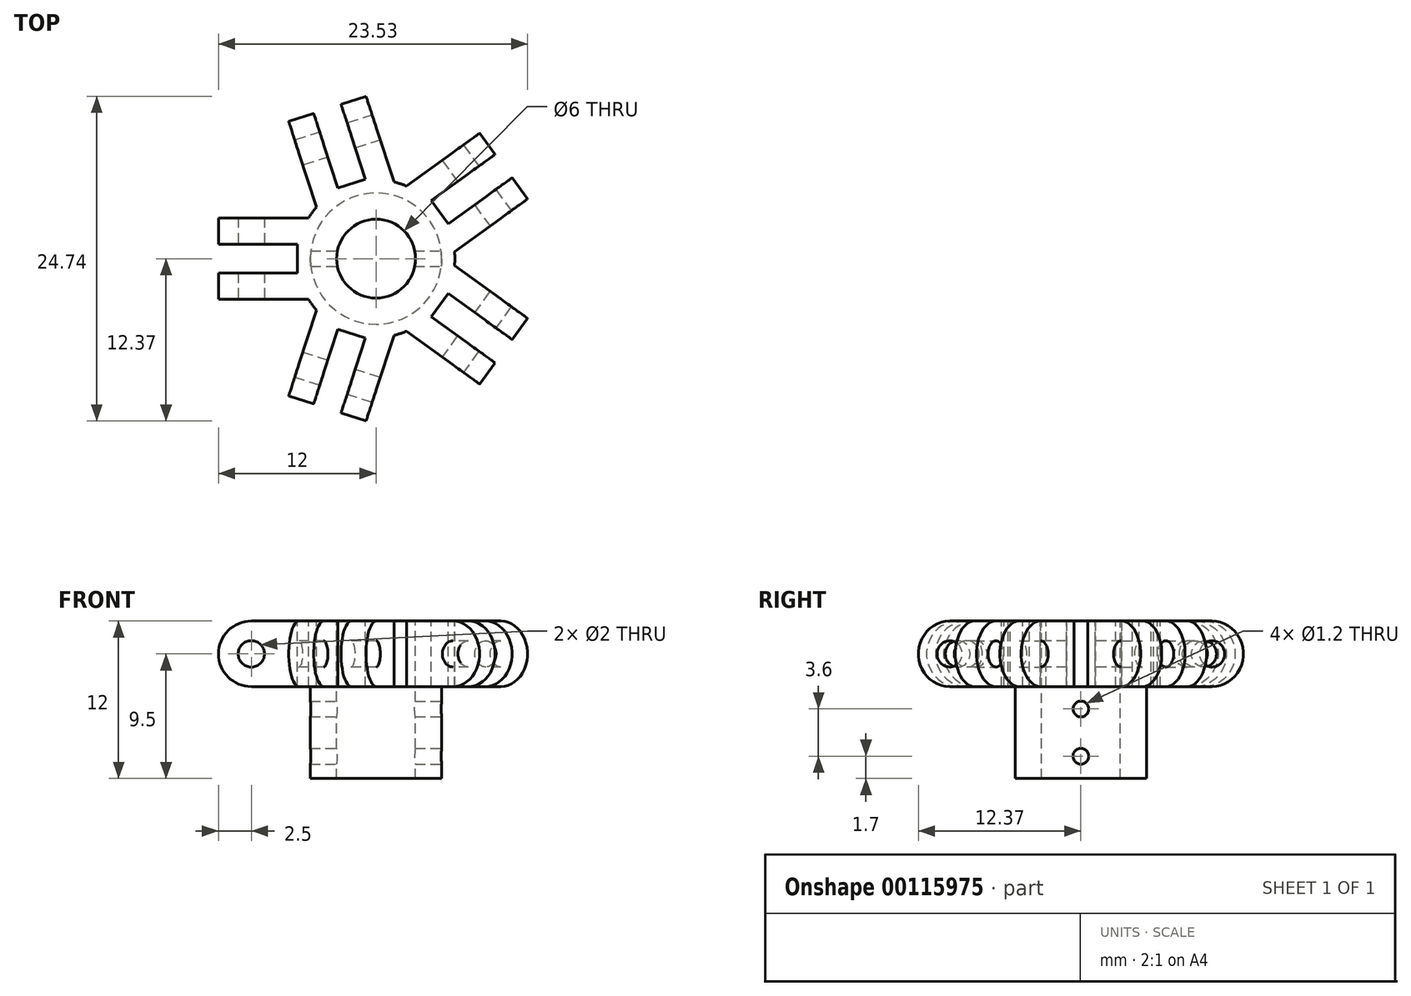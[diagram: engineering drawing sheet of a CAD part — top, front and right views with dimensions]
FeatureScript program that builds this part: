
annotation { "Feature Type Name" : "Feature", "Feature Type Description" : "" }
export const myFeature = defineFeature(function(context is Context, id is Id, definition is map)
    precondition{}
    {
        {
            var Q0;
            Q0=qCreatedBy(makeId("Front.planeOp"),FACE);
            var sketch = newSketch(context, id + "F0", { "sketchPlane" : qUnion([Q0])});
            skLineSegment(sketch, "E0", {"start": v(-3, 5) * mm, "end": v(-6, 5) * mm});
            skLineSegment(sketch, "E1", {"start": v(-6, 5) * mm, "end": v(-6, 0) * mm});
            skLineSegment(sketch, "E2", {"start": v(-6, 0) * mm, "end": v(-5, 0) * mm});
            skLineSegment(sketch, "E3", {"start": v(-5, 0) * mm, "end": v(-5, -7) * mm});
            skLineSegment(sketch, "E4", {"start": v(-5, -7) * mm, "end": v(-3, -7) * mm});
            skLineSegment(sketch, "E5", {"start": v(-3, -7) * mm, "end": v(-3, 5) * mm});
            skLineSegment(sketch, "E6", {"start": v(0, 11.9) * mm, "end": v(0, -21.79) * mm, "construction": true});
            skSolve(sketch);
        }
        {
            var Q0;
            Q0 = qSketchRegion(id + "F0", true);
            var Q1;
            Q1=sQuery(id+"F0.wireOp",EDGE,"E6");
            revolve(context, id + "F1", {"entities" : qUnion([Q0]), "axis" : qUnion([Q1]), "revolveType" : RevolveType.FULL});
        }
        {
            var Q0;
            Q0=qCreatedBy(makeId("Front.planeOp"),FACE);
            var sketch = newSketch(context, id + "F2", { "sketchPlane" : qUnion([Q0])});
            skLineSegment(sketch, "E7", {"start": v(-9.5, 5) * mm, "end": v(-5, 5) * mm});
            skLineSegment(sketch, "E8", {"start": v(-5, 5) * mm, "end": v(-5, 0) * mm});
            skLineSegment(sketch, "E9", {"start": v(-5, 0) * mm, "end": v(-9.5, 0) * mm});
            skLineSegment(sketch, "E10", {"start": v(-9.5, 0) * mm, "end": v(-9.5, 5) * mm, "construction": true});
            skArc(sketch, "E11", {"start": v(-9.5, 5) * mm, "mid": v(-12, 2.5) * mm, "end": v(-9.5, 0) * mm});
            skCircle(sketch, "E12", {"center": v(-9.5, 2.5) * mm, "radius": 2.5 * mm});
            skSolve(sketch);
        }
        {
            var Q0;
            Q0 = qSketchRegion(id + "F2", true);
            extrude(context, id + "F3", {"entities" : qUnion([Q0]), "endBound" : BoundingType.SYMMETRIC, "depth" : 6.2 * mm});
        }
        {
            var Q0;
            Q0=makeQuery(id+"F3.opExtrude","CAP_FACE",FACE,{"disambiguationData":[OSD([sQuery(id+"F2.wireOp",EDGE,"E7"),sQuery(id+"F2.wireOp",EDGE,"E8"),sQuery(id+"F2.wireOp",EDGE,"E9"),sQuery(id+"F2.wireOp",EDGE,"E12")])],"isStart":false});
            var sketch = newSketch(context, id + "F4", { "sketchPlane" : qUnion([Q0])});
            skCircle(sketch, "E13", {"center": v(-9.5, 2.5) * mm, "radius": 1 * mm});
            skSolve(sketch);
        }
        {
            var Q0;
            Q0=makeQuery(id+"F4.imprint","IMPRINT",FACE,{"disambiguationData":[TD([[makeQuery(id+"F4.imprint","IMPRINT",EDGE,{"derivedFrom":sQuery(id+"F4.wireOp",EDGE,"E13")}),1.0]])]});
            extrude(context, id + "F5", {"entities" : qUnion([Q0]), "operationType" : NewBodyOperationType.REMOVE, "endBound" : BoundingType.THROUGH_ALL, "oppositeDirection" : true, "depth" : 25 * mm});
        }
        {
            var Q0;
            Q0=makeQuery(id+"F3.opExtrude","SWEPT_FACE",FACE,{"disambiguationData":[OSD([sQuery(id+"F2.wireOp",EDGE,"E7")])]});
            var sketch = newSketch(context, id + "F6", { "sketchPlane" : qUnion([Q0])});
            skLineSegment(sketch, "E14.bottom", {"start": v(-13, 1.1) * mm, "end": v(-6, 1.1) * mm});
            skLineSegment(sketch, "E14.top", {"start": v(-13, -1.1) * mm, "end": v(-6, -1.1) * mm});
            skLineSegment(sketch, "E14.left", {"start": v(-13, 1.1) * mm, "end": v(-13, -1.1) * mm});
            skLineSegment(sketch, "E14.right", {"start": v(-6, 1.1) * mm, "end": v(-6, -1.1) * mm});
            skSolve(sketch);
        }
        {
            var Q0;
            Q0 = qSketchRegion(id + "F6", true);
            extrude(context, id + "F7", {"entities" : qUnion([Q0]), "operationType" : NewBodyOperationType.REMOVE, "oppositeDirection" : true, "depth" : 25 * mm});
        }
        {
            var Q0;
            Q0=makeQuery(id+"F3.opExtrude","SWEPT_BODY",BODY,{"disambiguationData":[OSD([sQuery(id+"F2.wireOp",EDGE,"E7"),sQuery(id+"F2.wireOp",EDGE,"E8"),sQuery(id+"F2.wireOp",EDGE,"E9"),sQuery(id+"F2.wireOp",EDGE,"E11"),sQuery(id+"F2.wireOp",EDGE,"E12")])]});
            var Q1;
            Q1=makeQuery(id+"F1.opRevolve","SWEPT_FACE",FACE,{"disambiguationData":[OSD([sQuery(id+"F0.wireOp",EDGE,"E5")])]});
            circularPattern(context, id + "F8", {"operationType" : NewBodyOperationType.ADD, "entities" : qUnion([Q0]), "axis" : qUnion([Q1]), "angle" : 360 * degree, "instanceCount" : 5, "equalSpace" : true});
        }
        {
            var Q0;
            Q0=qCreatedBy(makeId("Right.planeOp"),FACE);
            var sketch = newSketch(context, id + "F9", { "sketchPlane" : qUnion([Q0])});
            skCircle(sketch, "E15", {"center": v(0, -1.7) * mm, "radius": 0.6 * mm});
            skCircle(sketch, "E16", {"center": v(0, -5.3) * mm, "radius": 0.6 * mm});
            skLineSegment(sketch, "E17", {"start": v(0, -5.3) * mm, "end": v(0, -7) * mm, "construction": true});
            skLineSegment(sketch, "E18", {"start": v(0, -1.7) * mm, "end": v(0, 0) * mm, "construction": true});
            skSolve(sketch);
        }
        {
            var Q0;
            Q0 = qSketchRegion(id + "F9", true);
            extrude(context, id + "F10", {"entities" : qUnion([Q0]), "operationType" : NewBodyOperationType.REMOVE, "endBound" : BoundingType.THROUGH_ALL, "oppositeDirection" : true, "depth" : 25 * mm, "hasSecondDirection" : true, "secondDirectionBound" : SecondDirectionBoundingType.THROUGH_ALL, "secondDirectionOppositeDirection" : false, "secondDirectionDepth" : 25 * mm});
        }
    });
